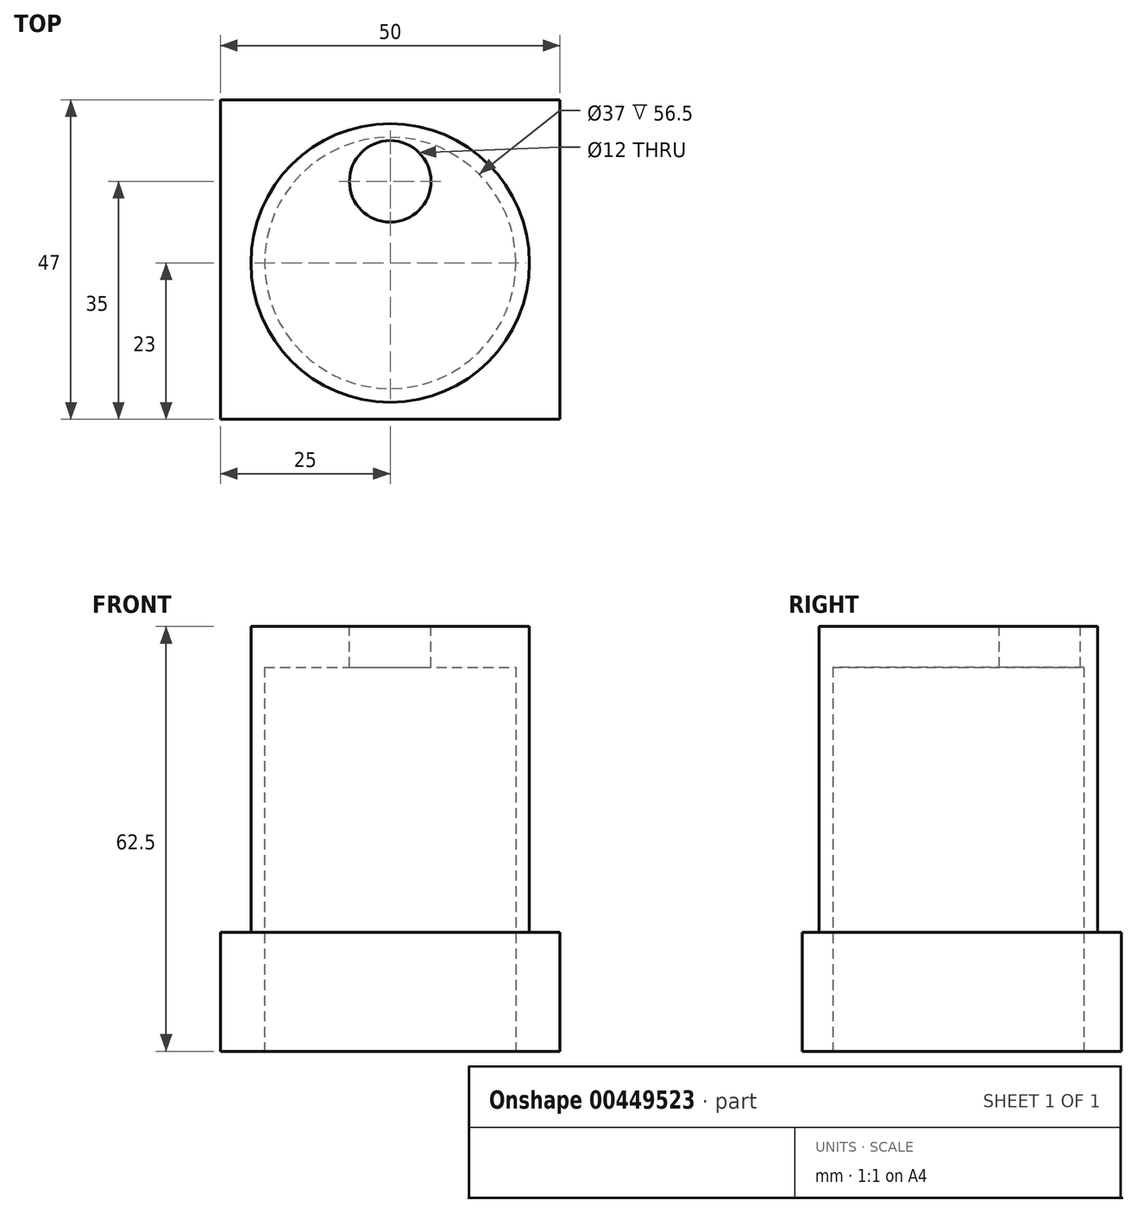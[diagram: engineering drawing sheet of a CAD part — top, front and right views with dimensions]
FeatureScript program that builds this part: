
annotation { "Feature Type Name" : "Feature", "Feature Type Description" : "" }
export const myFeature = defineFeature(function(context is Context, id is Id, definition is map)
    precondition{}
    {
        {
            var Q0;
            Q0=qCreatedBy(makeId("Top.planeOp"),FACE);
            var sketch = newSketch(context, id + "F0", { "sketchPlane" : qUnion([Q0])});
            skLineSegment(sketch, "E0.bottom", {"start": v(0, 0) * mm, "end": v(50, 0) * mm});
            skLineSegment(sketch, "E0.top", {"start": v(0, 47) * mm, "end": v(50, 47) * mm});
            skLineSegment(sketch, "E0.left", {"start": v(0, 0) * mm, "end": v(0, 47) * mm});
            skLineSegment(sketch, "E0.right", {"start": v(50, 0) * mm, "end": v(50, 47) * mm});
            skSolve(sketch);
        }
        {
            var Q0;
            Q0=makeQuery(id+"F0.imprint","IMPRINT",FACE,{"disambiguationData":[TD([[makeQuery(id+"F0.imprint","IMPRINT",EDGE,{"derivedFrom":sQuery(id+"F0.wireOp",EDGE,"E0.bottom")}),1.0]])]});
            extrude(context, id + "F1", {"entities" : qUnion([Q0]), "depth" : 17.5 * mm});
        }
        {
            var Q0;
            Q0=makeQuery(id+"F1.opExtrude","CAP_FACE",FACE,{"disambiguationData":[OSD([sQuery(id+"F0.wireOp",EDGE,"E0.bottom"),sQuery(id+"F0.wireOp",EDGE,"E0.top"),sQuery(id+"F0.wireOp",EDGE,"E0.left"),sQuery(id+"F0.wireOp",EDGE,"E0.right")])],"isStart":false});
            var sketch = newSketch(context, id + "F2", { "sketchPlane" : qUnion([Q0])});
            skPoint(sketch, "E1", {"position": v(25, 23) * mm});
            skCircle(sketch, "E2", {"center": v(25, 23) * mm, "radius": 20.5 * mm});
            skSolve(sketch);
        }
        {
            var Q0;
            Q0 = qSketchRegion(id + "F2", true);
            var Q1;
            Q1=makeQuery(id+"F2.imprint","IMPRINT",FACE,{"disambiguationData":[TD([[makeQuery(id+"F2.imprint","IMPRINT",EDGE,{"derivedFrom":sQuery(id+"F2.wireOp",EDGE,"E2")}),1.0]])]});
            extrude(context, id + "F3", {"entities" : qUnion([Q0, Q1]), "operationType" : NewBodyOperationType.ADD, "depth" : 45 * mm});
        }
        {
            var Q0;
            Q0=makeQuery(id+"F1.opExtrude","CAP_FACE",FACE,{"disambiguationData":[OSD([sQuery(id+"F0.wireOp",EDGE,"E0.bottom"),sQuery(id+"F0.wireOp",EDGE,"E0.top"),sQuery(id+"F0.wireOp",EDGE,"E0.left"),sQuery(id+"F0.wireOp",EDGE,"E0.right")])],"isStart":true});
            var sketch = newSketch(context, id + "F4", { "sketchPlane" : qUnion([Q0])});
            skPoint(sketch, "E3", {"position": v(25, -23) * mm});
            skCircle(sketch, "E4", {"center": v(25, -23) * mm, "radius": 18.5 * mm});
            skSolve(sketch);
        }
        {
            var Q0;
            Q0 = qSketchRegion(id + "F4", true);
            var Q1;
            Q1=makeQuery(id+"F4.imprint","IMPRINT",FACE,{"disambiguationData":[TD([[makeQuery(id+"F4.imprint","IMPRINT",EDGE,{"derivedFrom":sQuery(id+"F4.wireOp",EDGE,"E4")}),1.0]])]});
            extrude(context, id + "F5", {"entities" : qUnion([Q0, Q1]), "operationType" : NewBodyOperationType.REMOVE, "oppositeDirection" : true, "depth" : 56.5 * mm});
        }
        {
            var Q0;
            Q0=makeQuery(id+"F3.opExtrude","CAP_FACE",FACE,{"disambiguationData":[OSD([sQuery(id+"F2.wireOp",EDGE,"E2")])],"isStart":false});
            var sketch = newSketch(context, id + "F6", { "sketchPlane" : qUnion([Q0])});
            skPoint(sketch, "E5", {"position": v(25, 23) * mm});
            skPoint(sketch, "E6", {"position": v(25, 35) * mm});
            skCircle(sketch, "E7", {"center": v(25, 35) * mm, "radius": 6 * mm});
            skSolve(sketch);
        }
        {
            var Q0;
            Q0 = qSketchRegion(id + "F6", true);
            var Q1;
            Q1=makeQuery(id+"F6.imprint","IMPRINT",FACE,{"disambiguationData":[TD([[makeQuery(id+"F6.imprint","IMPRINT",EDGE,{"derivedFrom":sQuery(id+"F6.wireOp",EDGE,"E7")}),1.0]])]});
            extrude(context, id + "F7", {"entities" : qUnion([Q0, Q1]), "operationType" : NewBodyOperationType.REMOVE, "oppositeDirection" : true, "depth" : 25 * mm});
        }
    });
